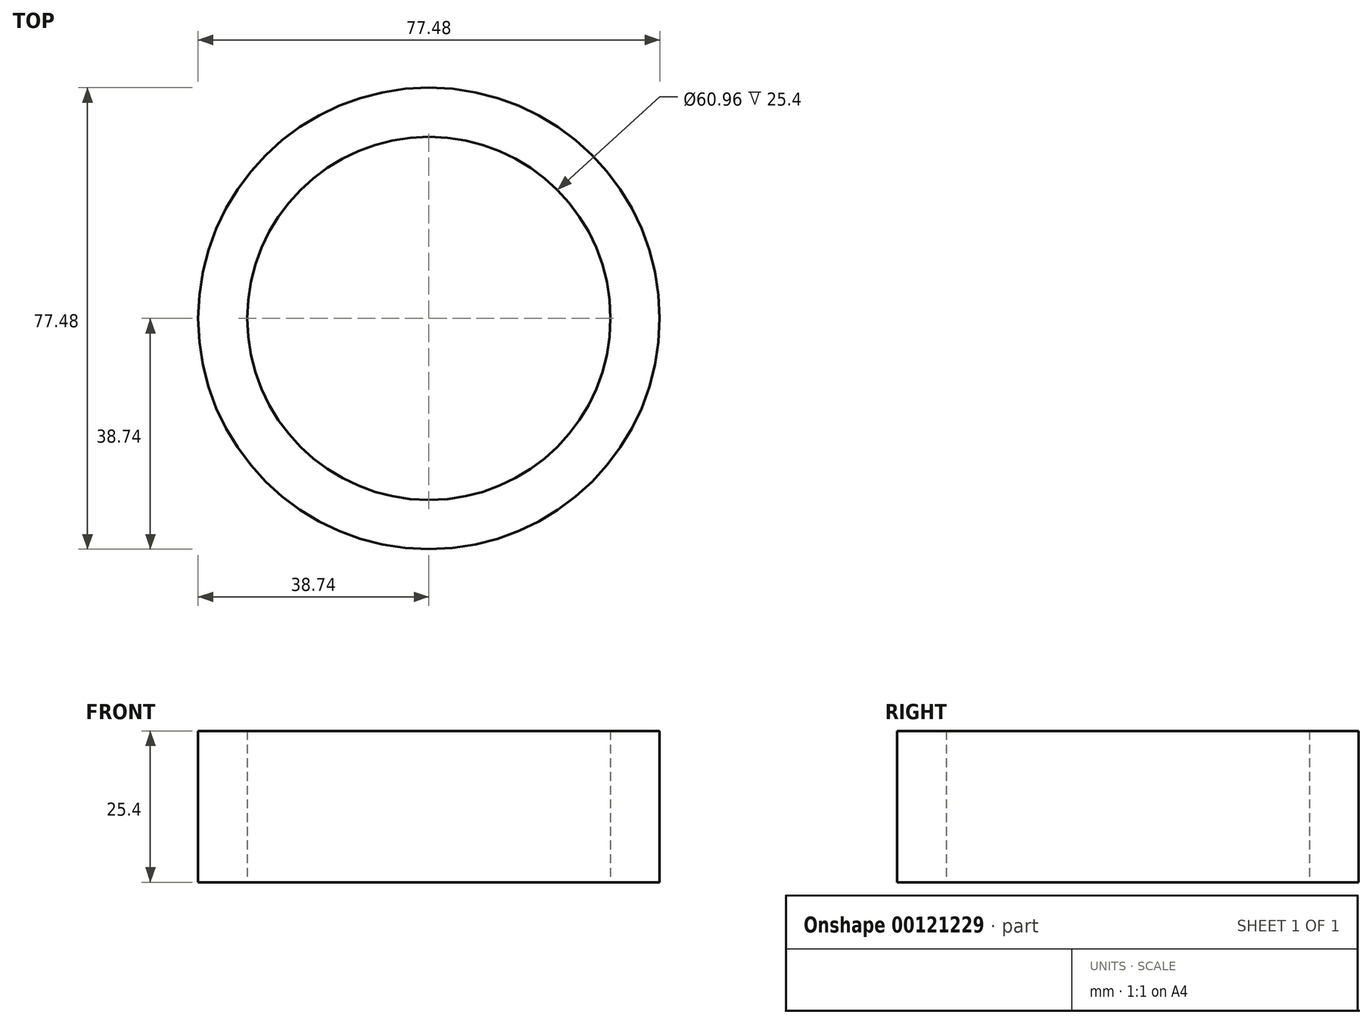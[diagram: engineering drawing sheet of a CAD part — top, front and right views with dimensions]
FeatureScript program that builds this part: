
annotation { "Feature Type Name" : "Feature", "Feature Type Description" : "" }
export const myFeature = defineFeature(function(context is Context, id is Id, definition is map)
    precondition{}
    {
        {
            var Q0;
            Q0=qCreatedBy(makeId("Top.planeOp"),FACE);
            var sketch = newSketch(context, id + "F0", { "sketchPlane" : qUnion([Q0])});
            skCircle(sketch, "E0", {"center": v(0, 0) * mm, "radius": 30.48 * mm});
            skCircle(sketch, "E1", {"center": v(0, 0) * mm, "radius": 38.73 * mm});
            skSolve(sketch);
        }
        {
            var Q0;
            Q0=makeQuery(id+"F0.imprint","IMPRINT",FACE,{"disambiguationData":[TD([[makeQuery(id+"F0.imprint","IMPRINT",EDGE,{"derivedFrom":sQuery(id+"F0.wireOp",EDGE,"E0")}),-1.0]])]});
            extrude(context, id + "F1", {"entities" : qUnion([Q0]), "depth" : 25.4 * mm});
        }
    });
